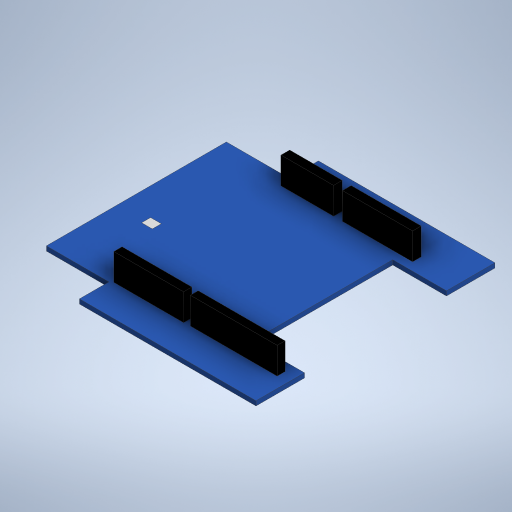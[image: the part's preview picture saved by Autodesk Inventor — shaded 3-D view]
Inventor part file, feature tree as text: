
AUTODESK INVENTOR PART (.ipt)
format: ipt  version: 2023 (Build 270158000, 158)  size: 485,376 bytes
history: native  units: mm
features: extrude x4, projected_geometry x4, sketch x2, other x1
ambient origin geometry x8: Origin, YZ Plane, XZ Plane, XY Plane, X Axis, Y Axis, Z Axis, Center Point
bodies: Body1 (feature_tree)
feature tree (11):
  sketch  "Esquisse1"
  extrude  "Extrusion2"  Depth=1.3mm TaperAngle=0.0deg
  extrude  "Extrusion3"  Depth=9.0mm TaperAngle=0.0deg
  extrude  "Extrusion4"  Depth=1.3001mm TaperAngle=0.0deg
  extrude  "Extrusion5"  Depth=1.0mm
  other  "Image1"
  sketch  "Esquisse2"
  projected_geometry  "Boucle projetée1"
  projected_geometry  "Boucle projetée2"
  projected_geometry  "Boucle projetée3"
  projected_geometry  "Boucle projetée4"
